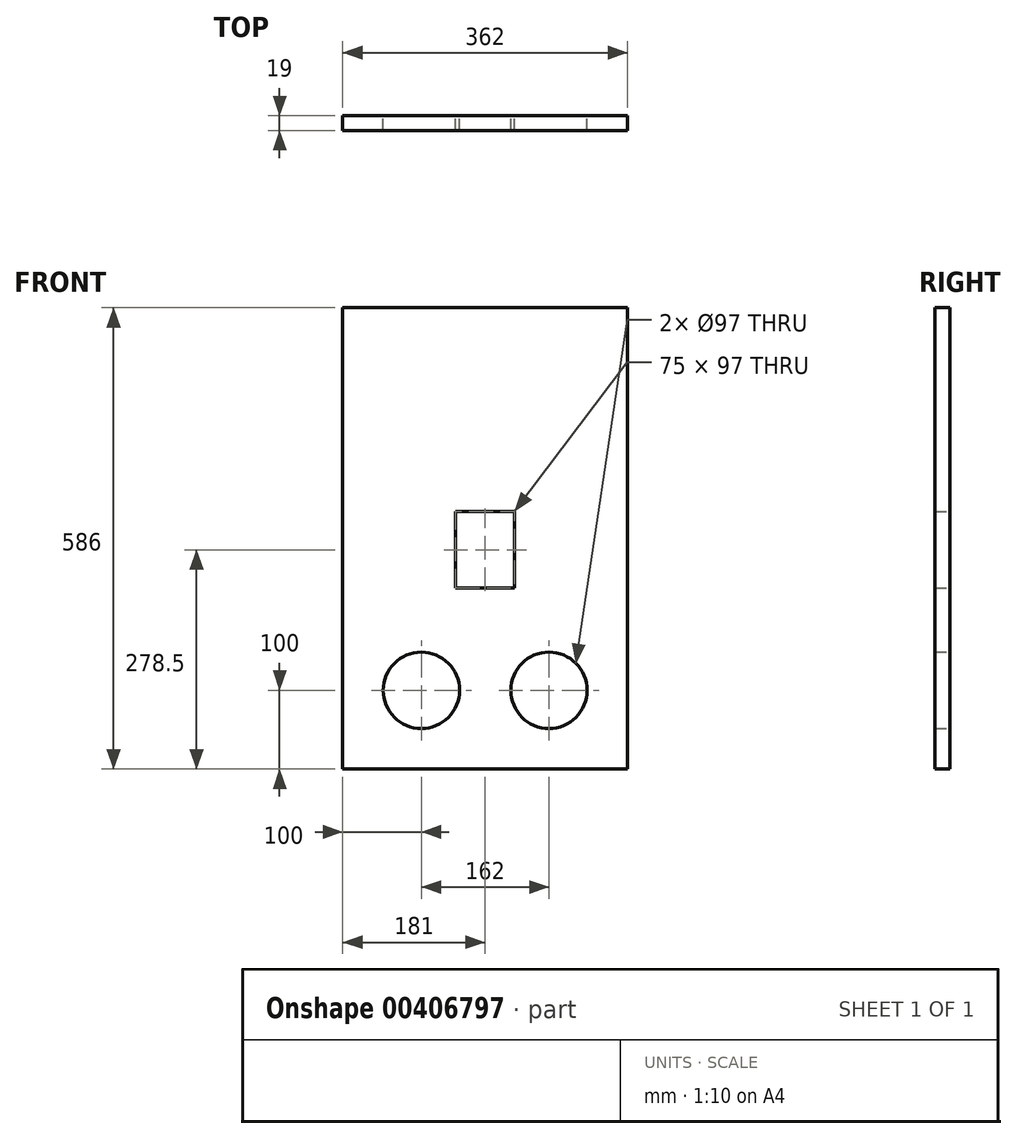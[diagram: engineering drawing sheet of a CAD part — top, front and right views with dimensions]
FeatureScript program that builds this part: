
annotation { "Feature Type Name" : "Feature", "Feature Type Description" : "" }
export const myFeature = defineFeature(function(context is Context, id is Id, definition is map)
    precondition{}
    {
        {
            var Q0;
            Q0=qCreatedBy(makeId("Front.planeOp"),FACE);
            var sketch = newSketch(context, id + "F0", { "sketchPlane" : qUnion([Q0])});
            skLineSegment(sketch, "E0.bottom", {"start": v(0, 0) * mm, "end": v(362, 0) * mm});
            skLineSegment(sketch, "E0.top", {"start": v(0, 586) * mm, "end": v(362, 586) * mm});
            skLineSegment(sketch, "E0.left", {"start": v(0, 0) * mm, "end": v(0, 586) * mm});
            skLineSegment(sketch, "E0.right", {"start": v(362, 0) * mm, "end": v(362, 586) * mm});
            skCircle(sketch, "E1", {"center": v(100, 100) * mm, "radius": 48.5 * mm});
            skCircle(sketch, "E2", {"center": v(262, 100) * mm, "radius": 48.5 * mm});
            skLineSegment(sketch, "E3.bottom", {"start": v(218.5, 327) * mm, "end": v(143.5, 327) * mm});
            skLineSegment(sketch, "E3.top", {"start": v(218.5, 230) * mm, "end": v(143.5, 230) * mm});
            skLineSegment(sketch, "E3.left", {"start": v(218.5, 327) * mm, "end": v(218.5, 230) * mm});
            skLineSegment(sketch, "E3.right", {"start": v(143.5, 327) * mm, "end": v(143.5, 230) * mm});
            skPoint(sketch, "E3.middle", {"position": v(181, 278.5) * mm});
            skSolve(sketch);
        }
        {
            var Q0;
            Q0=makeQuery(id+"F0.imprint","IMPRINT",FACE,{"disambiguationData":[TD([[makeQuery(id+"F0.imprint","IMPRINT",EDGE,{"derivedFrom":sQuery(id+"F0.wireOp",EDGE,"E0.bottom")}),1.0]])]});
            extrude(context, id + "F1", {"entities" : qUnion([Q0]), "depth" : 19 * mm, "offsetDistance" : 25 * mm});
        }
    });
